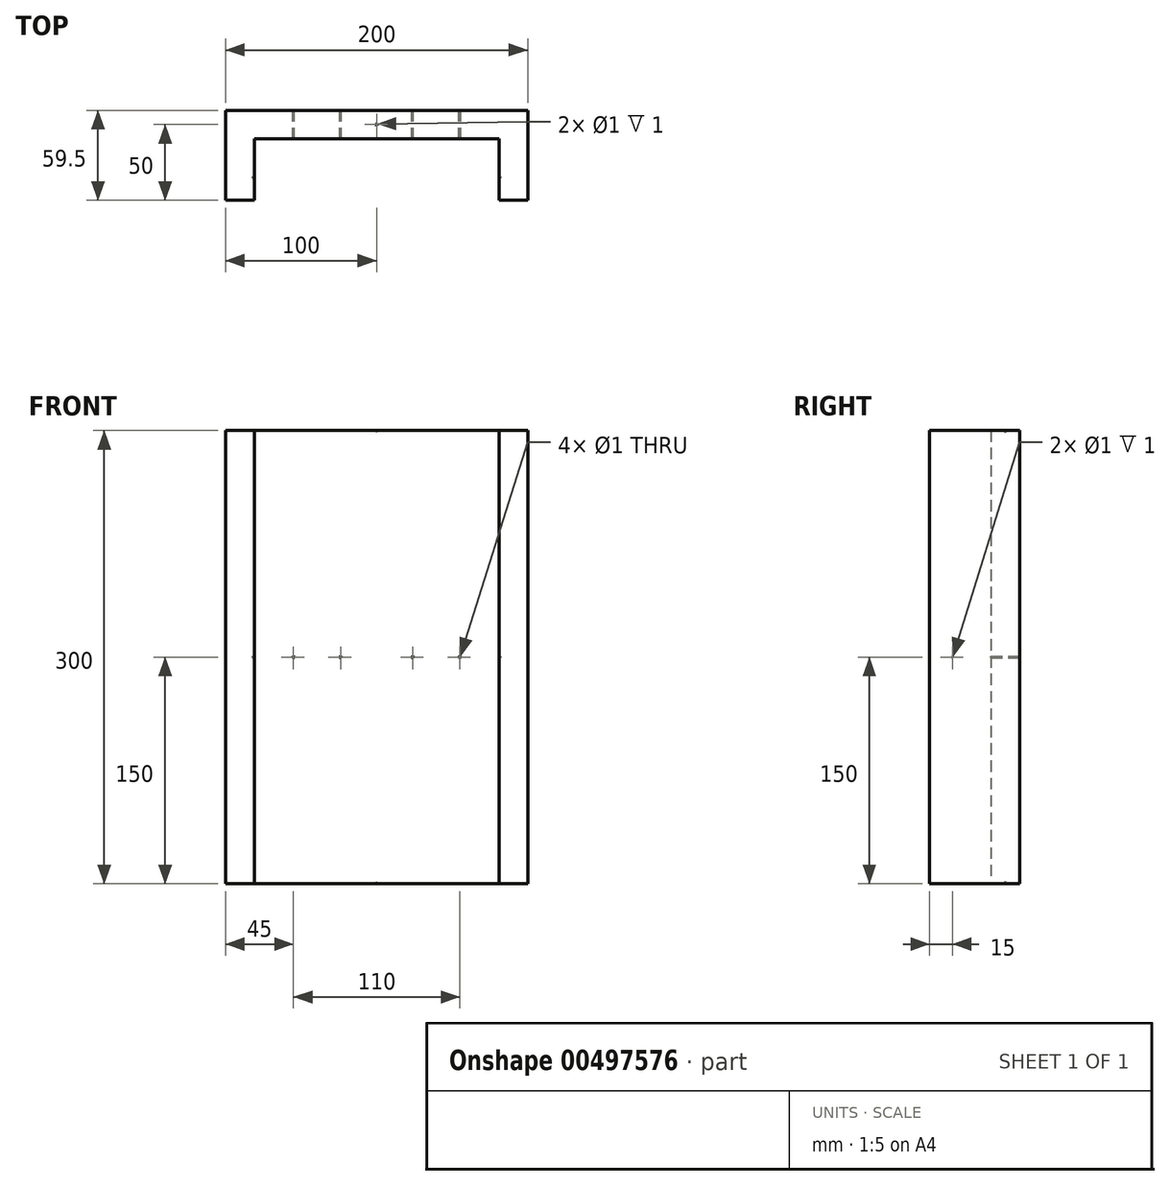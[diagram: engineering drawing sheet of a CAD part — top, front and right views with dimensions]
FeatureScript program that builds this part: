
annotation { "Feature Type Name" : "Feature", "Feature Type Description" : "" }
export const myFeature = defineFeature(function(context is Context, id is Id, definition is map)
    precondition{}
    {
        {
            var Q0;
            Q0=qCreatedBy(makeId("Front.planeOp"),FACE);
            var sketch = newSketch(context, id + "F0", { "sketchPlane" : qUnion([Q0])});
            skLineSegment(sketch, "E0.bottom", {"start": v(0, 0) * mm, "end": v(200, 0) * mm});
            skLineSegment(sketch, "E0.top", {"start": v(0, 300) * mm, "end": v(200, 300) * mm});
            skLineSegment(sketch, "E0.left", {"start": v(0, 0) * mm, "end": v(0, 300) * mm});
            skLineSegment(sketch, "E0.right", {"start": v(200, 0) * mm, "end": v(200, 300) * mm});
            skPoint(sketch, "E1.centerSnap0", {"position": v(200, 150) * mm});
            skLineSegment(sketch, "E2", {"start": v(100, 300) * mm, "end": v(100, 0) * mm, "construction": true});
            skCircle(sketch, "E3", {"center": v(45, 150) * mm, "radius": 0.5 * mm});
            skPoint(sketch, "E3.centerSnap0", {"position": v(100, 150) * mm});
            skCircle(sketch, "E4.MirrorC", {"center": v(155, 150) * mm, "radius": 0.5 * mm});
            skCircle(sketch, "E5", {"center": v(123.85, 150) * mm, "radius": 0.5 * mm});
            skCircle(sketch, "E6.MirrorC", {"center": v(76.15, 150) * mm, "radius": 0.5 * mm});
            skSolve(sketch);
        }
        {
            var Q0;
            Q0=makeQuery(id+"F0.imprint","IMPRINT",FACE,{"disambiguationData":[TD([[makeQuery(id+"F0.imprint","IMPRINT",EDGE,{"derivedFrom":sQuery(id+"F0.wireOp",EDGE,"E0.bottom")}),1.0]])]});
            extrude(context, id + "F1", {"entities" : qUnion([Q0]), "depth" : 19 * mm, "offsetDistance" : 25.4 * mm});
        }
        {
            var Q0;
            Q0=makeQuery(id+"F1.opExtrude","CAP_FACE",FACE,{"disambiguationData":[OSD([sQuery(id+"F0.wireOp",EDGE,"E0.bottom"),sQuery(id+"F0.wireOp",EDGE,"E0.top"),sQuery(id+"F0.wireOp",EDGE,"E0.left"),sQuery(id+"F0.wireOp",EDGE,"E0.right"),sQuery(id+"F0.wireOp",EDGE,"E1"),sQuery(id+"F0.wireOp",EDGE,"7e8b525e-63c1-4edf-858b-1ded0e2b52450.MirrorC")])],"isStart":false});
            var sketch = newSketch(context, id + "F2", { "sketchPlane" : qUnion([Q0])});
            skLineSegment(sketch, "E7", {"start": v(100, 300) * mm, "end": v(100, 0) * mm, "construction": true});
            skLineSegment(sketch, "E8.bottom", {"start": v(0, 300) * mm, "end": v(19, 300) * mm});
            skLineSegment(sketch, "E8.top", {"start": v(0, 0) * mm, "end": v(19, 0) * mm});
            skLineSegment(sketch, "E8.left", {"start": v(0, 300) * mm, "end": v(0, 0) * mm});
            skLineSegment(sketch, "E8.right", {"start": v(19, 300) * mm, "end": v(19, 0) * mm});
            skLineSegment(sketch, "E9.MirrorCS", {"start": v(200, 0) * mm, "end": v(181, 0) * mm});
            skLineSegment(sketch, "E10.MirrorCS", {"start": v(200, 300) * mm, "end": v(181, 300) * mm});
            skLineSegment(sketch, "E11.MirrorCS", {"start": v(181, 300) * mm, "end": v(181, 0) * mm});
            skLineSegment(sketch, "E12.MirrorCS", {"start": v(200, 300) * mm, "end": v(200, 0) * mm});
            skSolve(sketch);
        }
        {
            var Q0;
            Q0 = qSketchRegion(id + "F2", true);
            extrude(context, id + "F3", {"entities" : qUnion([Q0]), "operationType" : NewBodyOperationType.ADD, "depth" : 40.5 * mm, "offsetDistance" : 25.4 * mm});
        }
        {
            var Q0;
            Q0=makeQuery(id+"F3.opExtrude","SWEPT_FACE",FACE,{"disambiguationData":[OSD([sQuery(id+"F2.wireOp",EDGE,"E8.right")])]});
            var sketch = newSketch(context, id + "F4", { "sketchPlane" : qUnion([Q0])});
            skCircle(sketch, "E13", {"center": v(-44.5, 150) * mm, "radius": 0.5 * mm});
            skPoint(sketch, "E13.centerSnap0", {"position": v(-59.5, 150) * mm});
            skSolve(sketch);
        }
        {
            var Q0;
            Q0 = qSketchRegion(id + "F4", true);
            extrude(context, id + "F5", {"entities" : qUnion([Q0]), "operationType" : NewBodyOperationType.REMOVE, "oppositeDirection" : true, "depth" : 1 * mm, "offsetDistance" : 25.4 * mm});
        }
        {
            var Q0;
            Q0=makeQuery(id+"F3.opExtrude","SWEPT_FACE",FACE,{"disambiguationData":[OSD([sQuery(id+"F2.wireOp",EDGE,"E11.MirrorCS")])]});
            var sketch = newSketch(context, id + "F6", { "sketchPlane" : qUnion([Q0])});
            skCircle(sketch, "E14", {"center": v(44.5, 150) * mm, "radius": 0.5 * mm});
            skPoint(sketch, "E14.centerSnap0", {"position": v(59.5, 150) * mm});
            skSolve(sketch);
        }
        {
            var Q0;
            Q0 = qSketchRegion(id + "F6", true);
            extrude(context, id + "F7", {"entities" : qUnion([Q0]), "operationType" : NewBodyOperationType.REMOVE, "oppositeDirection" : true, "depth" : 1 * mm, "offsetDistance" : 25.4 * mm});
        }
        {
            var Q0;
            Q0=makeQuery(id+"F3.boolean.opBoolean","MERGE",FACE,{"derivedFrom":[makeQuery(id+"F1.opExtrude","SWEPT_FACE",FACE,{"disambiguationData":[OSD([sQuery(id+"F0.wireOp",EDGE,"E0.bottom")])]}),makeQuery(id+"F3.opExtrude","SWEPT_FACE",FACE,{"disambiguationData":[OSD([sQuery(id+"F2.wireOp",EDGE,"E8.top")])]}),makeQuery(id+"F3.opExtrude","SWEPT_FACE",FACE,{"disambiguationData":[OSD([sQuery(id+"F2.wireOp",EDGE,"E9.MirrorCS")])]})]});
            var sketch = newSketch(context, id + "F8", { "sketchPlane" : qUnion([Q0])});
            skCircle(sketch, "E15", {"center": v(100, 9.5) * mm, "radius": 0.5 * mm});
            skPoint(sketch, "E15.centerSnap0", {"position": v(100, 0) * mm});
            skSolve(sketch);
        }
        {
            var Q0;
            Q0 = qSketchRegion(id + "F8", true);
            extrude(context, id + "F9", {"entities" : qUnion([Q0]), "operationType" : NewBodyOperationType.REMOVE, "oppositeDirection" : true, "depth" : 1 * mm, "offsetDistance" : 25.4 * mm});
        }
        {
            var Q0;
            Q0=makeQuery(id+"F3.boolean.opBoolean","MERGE",FACE,{"derivedFrom":[makeQuery(id+"F1.opExtrude","SWEPT_FACE",FACE,{"disambiguationData":[OSD([sQuery(id+"F0.wireOp",EDGE,"E0.top")])]}),makeQuery(id+"F3.opExtrude","SWEPT_FACE",FACE,{"disambiguationData":[OSD([sQuery(id+"F2.wireOp",EDGE,"E8.bottom")])]}),makeQuery(id+"F3.opExtrude","SWEPT_FACE",FACE,{"disambiguationData":[OSD([sQuery(id+"F2.wireOp",EDGE,"E10.MirrorCS")])]})]});
            var sketch = newSketch(context, id + "F10", { "sketchPlane" : qUnion([Q0])});
            skCircle(sketch, "E16", {"center": v(100, -9.5) * mm, "radius": 0.5 * mm});
            skPoint(sketch, "E16.centerSnap0", {"position": v(100, 0) * mm});
            skSolve(sketch);
        }
        {
            var Q0;
            Q0 = qSketchRegion(id + "F10", true);
            extrude(context, id + "F11", {"entities" : qUnion([Q0]), "operationType" : NewBodyOperationType.REMOVE, "oppositeDirection" : true, "depth" : 1 * mm, "offsetDistance" : 25.4 * mm});
        }
    });
